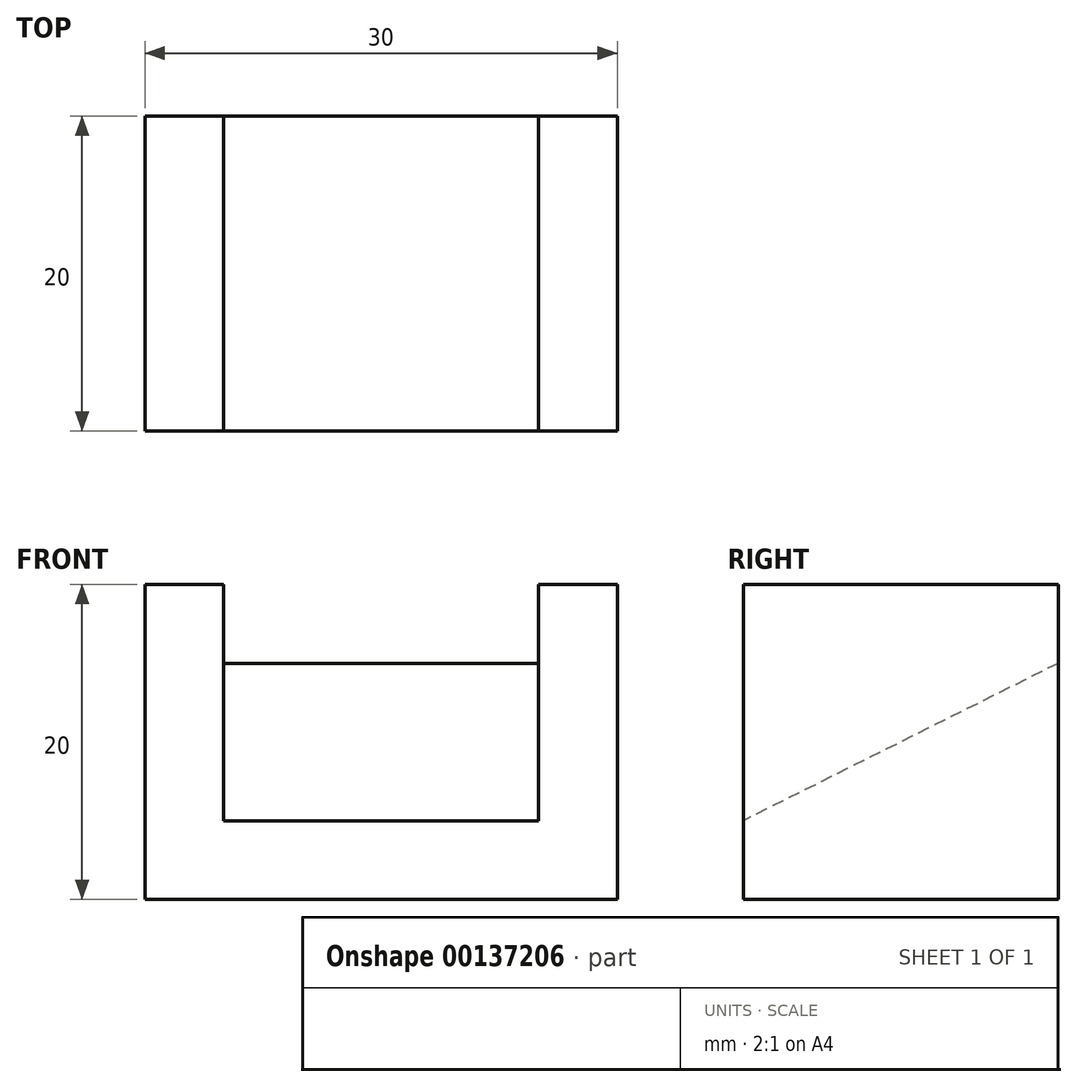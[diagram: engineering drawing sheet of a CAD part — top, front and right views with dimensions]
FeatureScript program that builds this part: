
annotation { "Feature Type Name" : "Feature", "Feature Type Description" : "" }
export const myFeature = defineFeature(function(context is Context, id is Id, definition is map)
    precondition{}
    {
        {
            var Q0;
            Q0=qCreatedBy(makeId("Front.planeOp"),FACE);
            var sketch = newSketch(context, id + "F0", { "sketchPlane" : qUnion([Q0])});
            skLineSegment(sketch, "E0.bottom", {"start": v(0, 0) * mm, "end": v(25, 0) * mm});
            skLineSegment(sketch, "E0.top", {"start": v(0, 20) * mm, "end": v(25, 20) * mm});
            skLineSegment(sketch, "E0.left", {"start": v(0, 0) * mm, "end": v(0, 20) * mm});
            skLineSegment(sketch, "E0.right", {"start": v(25, 0) * mm, "end": v(25, 20) * mm});
            skSolve(sketch);
        }
        {
            var Q0;
            Q0 = qSketchRegion(id + "F0", true);
            extrude(context, id + "F1", {"entities" : qUnion([Q0]), "depth" : 20 * mm});
        }
        {
            var Q0;
            Q0=makeQuery(id+"F1.opExtrude","SWEPT_FACE",FACE,{"disambiguationData":[OSD([sQuery(id+"F0.wireOp",EDGE,"E0.right")])]});
            var sketch = newSketch(context, id + "F2", { "sketchPlane" : qUnion([Q0])});
            skPoint(sketch, "E1.0", {"position": v(-20, 20) * mm});
            skPoint(sketch, "E2.0", {"position": v(0, 20) * mm});
            skLineSegment(sketch, "E3", {"start": v(-20, 20) * mm, "end": v(0, 20) * mm});
            skLineSegment(sketch, "E4", {"start": v(0, 20) * mm, "end": v(0, 15) * mm});
            skLineSegment(sketch, "E5", {"start": v(0, 15) * mm, "end": v(-20, 5) * mm});
            skLineSegment(sketch, "E6", {"start": v(-20, 5) * mm, "end": v(-20, 20) * mm});
            skSolve(sketch);
        }
        {
            var Q0;
            Q0 = qSketchRegion(id + "F2", true);
            extrude(context, id + "F3", {"entities" : qUnion([Q0]), "operationType" : NewBodyOperationType.REMOVE, "oppositeDirection" : true, "depth" : 20 * mm});
        }
        {
            var Q0;
            Q0=makeQuery(id+"F1.opExtrude","SWEPT_FACE",FACE,{"disambiguationData":[OSD([sQuery(id+"F0.wireOp",EDGE,"E0.right")])]});
            var sketch = newSketch(context, id + "F4", { "sketchPlane" : qUnion([Q0])});
            skPoint(sketch, "E7.0", {"position": v(-20, 20) * mm});
            skLineSegment(sketch, "E8.bottom", {"start": v(-20, 20) * mm, "end": v(0, 20) * mm});
            skLineSegment(sketch, "E8.top", {"start": v(-20, 0) * mm, "end": v(0, 0) * mm});
            skLineSegment(sketch, "E8.left", {"start": v(-20, 20) * mm, "end": v(-20, 0) * mm});
            skLineSegment(sketch, "E8.right", {"start": v(0, 20) * mm, "end": v(0, 0) * mm});
            skSolve(sketch);
        }
        {
            var Q0;
            Q0 = qSketchRegion(id + "F4", true);
            extrude(context, id + "F5", {"entities" : qUnion([Q0]), "operationType" : NewBodyOperationType.ADD, "depth" : 5 * mm});
        }
    });
